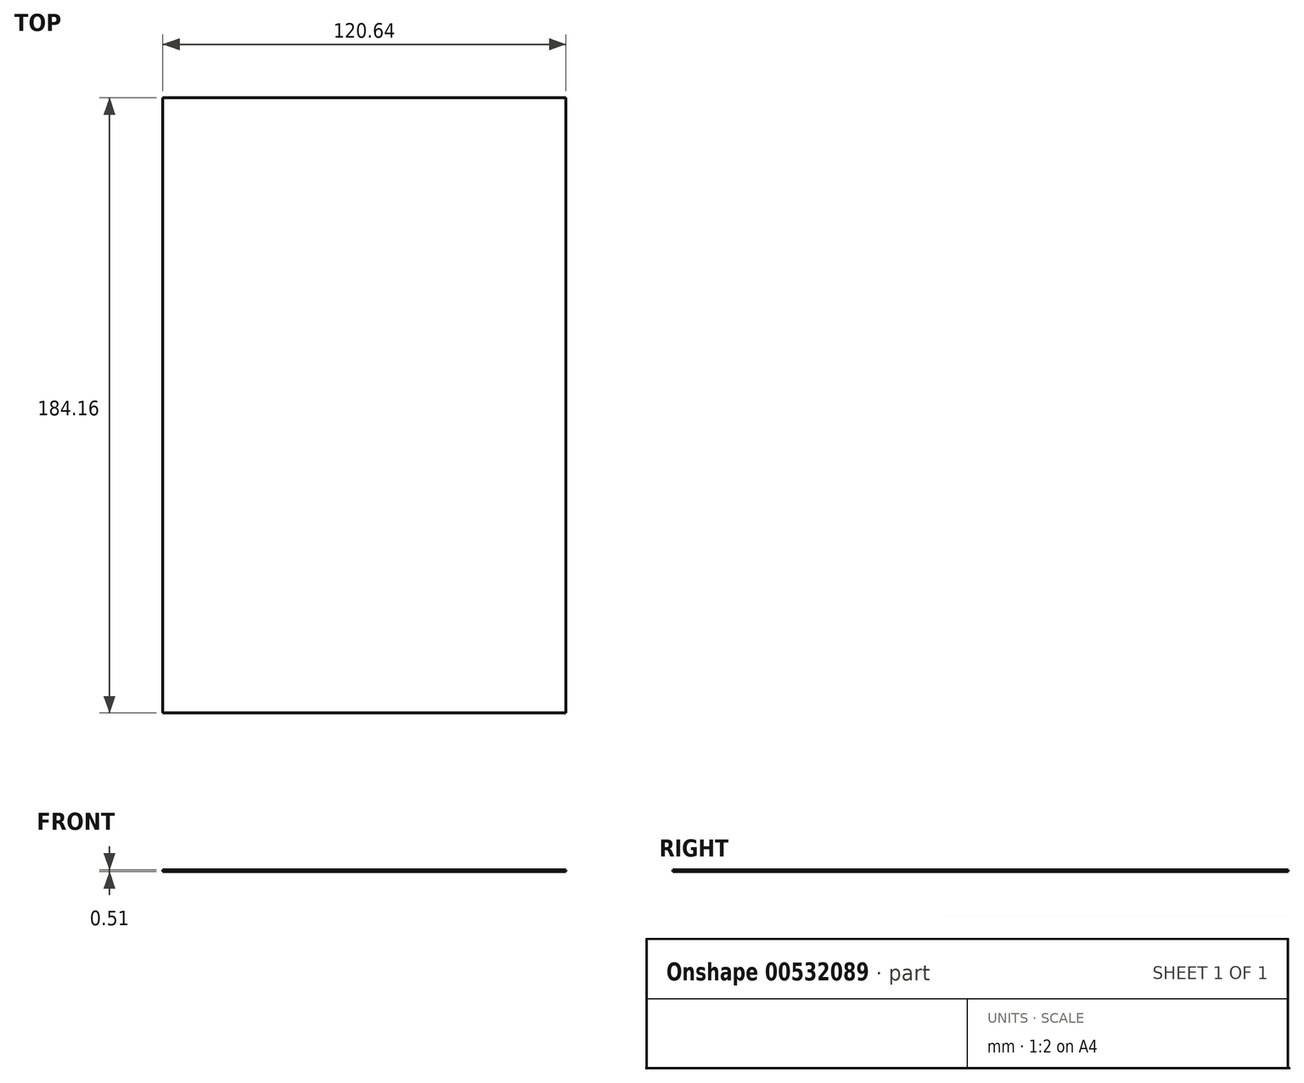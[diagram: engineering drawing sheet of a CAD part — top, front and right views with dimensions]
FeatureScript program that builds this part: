
annotation { "Feature Type Name" : "Feature", "Feature Type Description" : "" }
export const myFeature = defineFeature(function(context is Context, id is Id, definition is map)
    precondition{}
    {
        {
            var Q0;
            Q0=qCreatedBy(makeId("Top.planeOp"),FACE);
            var sketch = newSketch(context, id + "F0", { "sketchPlane" : qUnion([Q0])});
            skLineSegment(sketch, "E0.bottom", {"start": v(-60.33, 92.08) * mm, "end": v(60.33, 92.08) * mm});
            skLineSegment(sketch, "E0.top", {"start": v(-60.33, -92.07) * mm, "end": v(60.33, -92.08) * mm});
            skLineSegment(sketch, "E0.left", {"start": v(-60.32, 92.07) * mm, "end": v(-60.33, -92.07) * mm});
            skLineSegment(sketch, "E0.right", {"start": v(60.33, 92.07) * mm, "end": v(60.32, -92.07) * mm});
            skPoint(sketch, "E1.startSnap0", {"position": v(0, 92.08) * mm});
            skLineSegment(sketch, "E2", {"start": v(-60.33, 0) * mm, "end": v(60.33, 0) * mm, "construction": true});
            skLineSegment(sketch, "E3", {"start": v(0, 92.08) * mm, "end": v(0, -92.08) * mm, "construction": true});
            skSolve(sketch);
        }
        {
            var Q0;
            Q0 = qSketchRegion(id + "F0", true);
            extrude(context, id + "F1", {"entities" : qUnion([Q0]), "oppositeDirection" : true, "depth" : 0.5 * mm, "offsetDistance" : 25.4 * mm});
        }
    });
